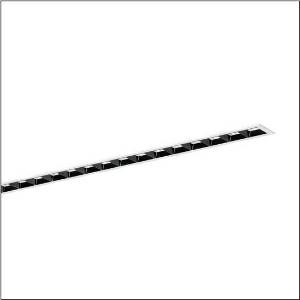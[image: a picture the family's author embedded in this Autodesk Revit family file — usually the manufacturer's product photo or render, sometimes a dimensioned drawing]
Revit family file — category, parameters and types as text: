
# Revit family: silica_r__21_51mx14tat4w_c2be
name_source: partatom
category: Lighting Fixtures
units: mm (PartAtom-declared; Revit-internal decimal feet)

## family parameters
Cut with Voids When Loaded = No
Host = Face
Light Source = No
Part Type = Normal
Room Calculation Point = No
Round Connector Dimension = Use Diameter
Shared = No

## types (1)
- --- (1 x LED, 3280 lm, 32.4 W, 6500K)
    Apparent Load = 32 VA
    CIE Flux Codes = 74 94 99 100 100
    Color Rendering = 80
    Color Temperature = 6500K
    Default Elevation = 1800 mm
    Description = Silica® 21, office luminaire, primary light control with darklight reflector, of PMMA, black, light emission: direct distribution, primary light characteristic: asymmetric, installation type: recessed, LED, rated luminous flux: 3.280lm, luminous efficacy: 96lm/W, light colour: 8tw, colour temperature: 2700..6500K, with terminal, 3+2-pole, max. 2.5mm², mains connection: 220..240V, AC, 50/60Hz, rated input power: 34.1W, luminaire housing, of aluminium, traffic white (RAL 9016), length: 1.228mm, width: 79mm, height: 53mm, protection rating (complete): IP20, insulation class (complete): insulation class I (protective earthing), certification: CE, permissible operating ambient temperature: 0..+35°C, standard: EN 50419, packaging unit: 1 piece
    Height = 0 mm  [stored 0 ft]
    Lamp = 1 x LED
    Lamp Light Flux = 3280 lm
    Lamp Power = 32.4 W
    Lamp count = 1
    Length = 1227 mm
    Luminous efficacy = 101 lm/W
    Manufacturer = Siteco
    ModVariant = No
    Model = 51MX14TAT4W
    Mounting Place = Ceiling
    Mounting Type = Recessed
    Number of Poles = 1
    OnlyDefault = Yes
    Power Factor = 1
    Product Name = Silica® 21
    Product group = office luminaire | ceiling recessed
    ProductGroupID = 400
    Protection Class = Protection class I
    Protection Degree = IP 20
    RLX_Detail_Level = 1
    RlxData = <blob elided: 35969 chars, md5=40608a16>
    Socket = socket
    Standby Power = 0 W
    System Light Flux = 3280 lm
    System Power = 32 W
    Type Comments = individual setting
    Type Image = l_1251632.jpg
    URL = http://relux.com
    VarID = @adj_046125
    Voltage = 0 V
    Weight = 0.00 kg
    Width = 79 mm

note: [stored X ft] marks values corroborated as IEEE doubles in the binary element streams (Revit-internal decimal feet)

## geometry (parser evidence)
native form markers: Blend x4, Sweep x10
no freeform markers — native parametric forms only
